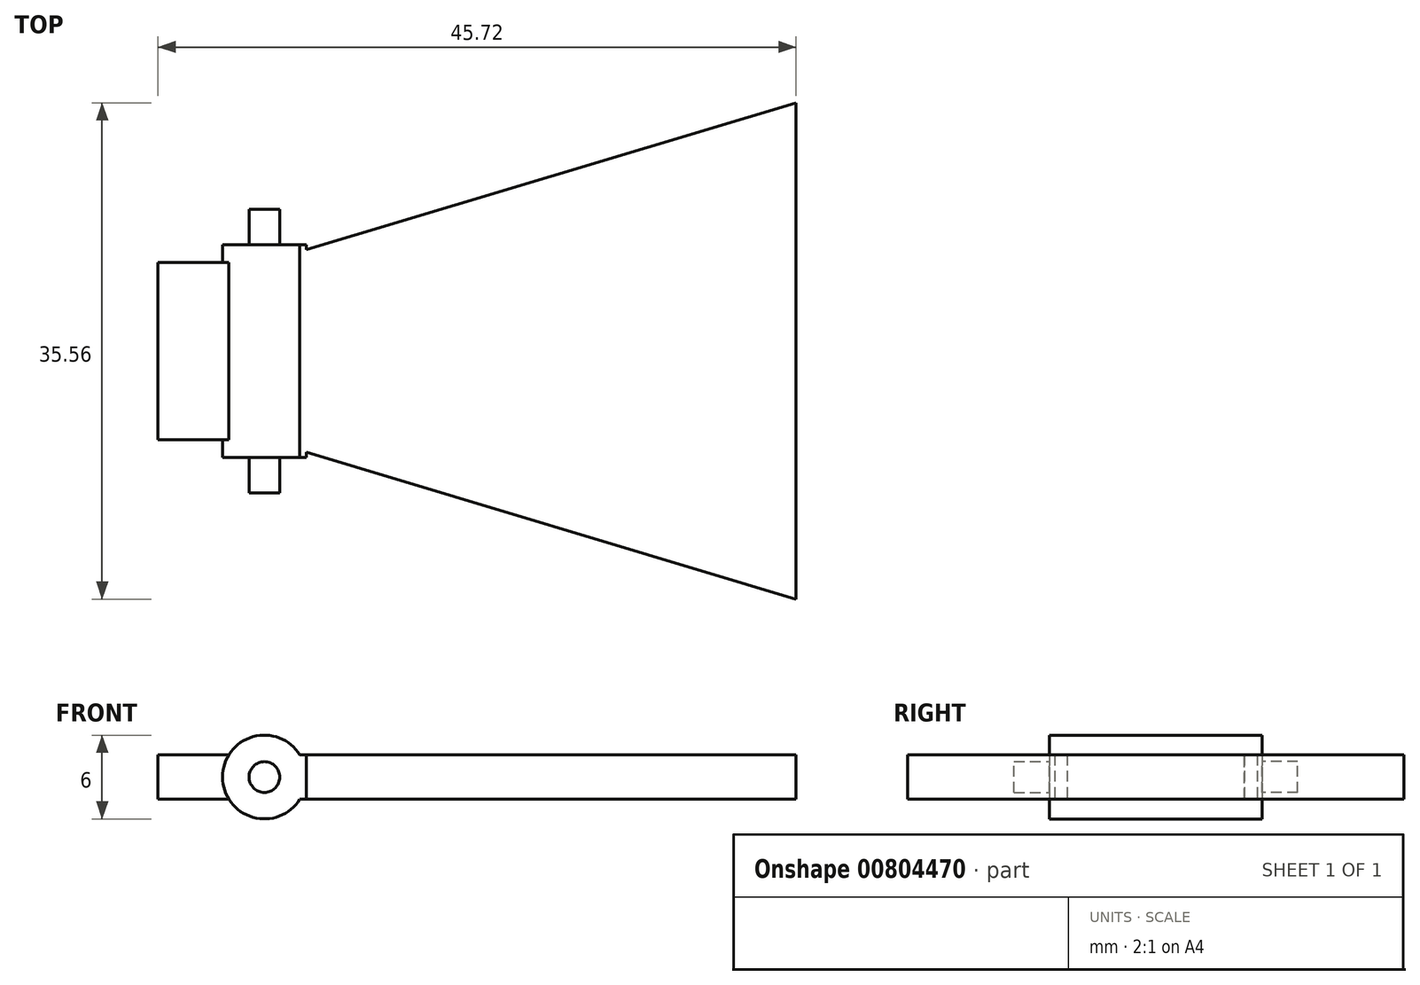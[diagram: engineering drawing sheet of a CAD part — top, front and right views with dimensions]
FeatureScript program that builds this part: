
annotation { "Feature Type Name" : "Feature", "Feature Type Description" : "" }
export const myFeature = defineFeature(function(context is Context, id is Id, definition is map)
    precondition{}
    {
        {
            var Q0;
            Q0=qCreatedBy(makeId("Top.planeOp"),FACE);
            var sketch = newSketch(context, id + "F0", { "sketchPlane" : qUnion([Q0])});
            skLineSegment(sketch, "E0", {"start": v(-25.02, 0) * mm, "end": v(-25.02, -6.35) * mm});
            skLineSegment(sketch, "E1", {"start": v(-25.02, -6.35) * mm, "end": v(13.08, -17.78) * mm});
            skLineSegment(sketch, "E2", {"start": v(13.08, -17.78) * mm, "end": v(13.08, 0) * mm});
            skLineSegment(sketch, "E3.MirrorCS", {"start": v(-25.02, 0) * mm, "end": v(-25.02, 6.35) * mm});
            skLineSegment(sketch, "E4.MirrorCS", {"start": v(-25.02, 6.35) * mm, "end": v(13.08, 17.78) * mm});
            skLineSegment(sketch, "E5.MirrorCS", {"start": v(13.08, 17.78) * mm, "end": v(13.08, 0) * mm});
            skLineSegment(sketch, "E6", {"start": v(-25.02, -6.35) * mm, "end": v(-32.64, -6.35) * mm});
            skLineSegment(sketch, "E7", {"start": v(-32.64, -6.35) * mm, "end": v(-32.64, 6.35) * mm});
            skLineSegment(sketch, "E8", {"start": v(-32.64, 6.35) * mm, "end": v(-25.02, 6.35) * mm});
            skLineSegment(sketch, "E9", {"start": v(-22.02, 6.35) * mm, "end": v(-22.02, -6.35) * mm});
            skLineSegment(sketch, "E10", {"start": v(-25.02, -6.35) * mm, "end": v(-25.02, -7.62) * mm});
            skLineSegment(sketch, "E11", {"start": v(-25.02, -7.62) * mm, "end": v(-22.02, -7.62) * mm});
            skLineSegment(sketch, "E12", {"start": v(-22.02, -7.62) * mm, "end": v(-22.02, -6.35) * mm});
            skLineSegment(sketch, "E13", {"start": v(-25.02, 6.35) * mm, "end": v(-22.02, 6.35) * mm});
            skLineSegment(sketch, "E14", {"start": v(-25.02, -6.35) * mm, "end": v(-22.02, -6.35) * mm});
            skLineSegment(sketch, "E15.MirrorCS", {"start": v(-25.02, 6.35) * mm, "end": v(-25.02, 7.62) * mm});
            skLineSegment(sketch, "E16.MirrorCS", {"start": v(-25.02, 7.62) * mm, "end": v(-22.02, 7.62) * mm});
            skLineSegment(sketch, "E17.MirrorCS", {"start": v(-22.02, 7.62) * mm, "end": v(-22.02, 6.35) * mm});
            skSolve(sketch);
        }
        {
            var Q0;
            Q0=makeQuery(id+"F0.imprint","IMPRINT",FACE,{"disambiguationData":[TD([[makeQuery(id+"F0.imprint","IMPRINT",EDGE,{"derivedFrom":sQuery(id+"F0.wireOp",EDGE,"E0")}),1.0]])]});
            var Q1;
            {var subQ0=sQuery(id+"F0.wireOp",EDGE,"E15.MirrorCS");Q1=makeQuery(id+"F0.imprint","IMPRINT",FACE,{"disambiguationData":[TD([[makeQuery(id+"F0.imprint","IMPRINT",EDGE,{"derivedFrom":subQ0}),-1.0]])]});}
            var Q2;
            {var subQ0=sQuery(id+"F0.wireOp",EDGE,"E10");Q2=makeQuery(id+"F0.imprint","IMPRINT",FACE,{"disambiguationData":[TD([[makeQuery(id+"F0.imprint","IMPRINT",EDGE,{"derivedFrom":subQ0}),1.0]])]});}
            var Q3;
            {var subQ0=sQuery(id+"F0.wireOp",EDGE,"E14");Q3=makeQuery(id+"F0.imprint","IMPRINT",FACE,{"disambiguationData":[TD([[makeQuery(id+"F0.imprint","IMPRINT",EDGE,{"derivedFrom":subQ0}),-1.0]])]});}
            var Q4;
            {var subQ0=sQuery(id+"F0.wireOp",EDGE,"E13");Q4=makeQuery(id+"F0.imprint","IMPRINT",FACE,{"disambiguationData":[TD([[makeQuery(id+"F0.imprint","IMPRINT",EDGE,{"derivedFrom":subQ0}),1.0]])]});}
            var Q5;
            Q5=sQuery(id+"F0.wireOp",EDGE,"E3.MirrorCS");
            revolve(context, id + "F1", {"surfaceOperationType" : NewSurfaceOperationType.NEW, "entities" : qUnion([Q0, Q1, Q2, Q3, Q4]), "axis" : qUnion([Q5]), "revolveType" : RevolveType.FULL});
        }
        {
            var Q0;
            Q0 = qSketchRegion(id + "F0", true);
            extrude(context, id + "F2", {"entities" : qUnion([Q0]), "operationType" : NewBodyOperationType.ADD, "endBound" : BoundingType.SYMMETRIC, "depth" : 3.17 * mm, "offsetDistance" : 25.4 * mm});
        }
        {
            var Q0;
            {var subQ0=sQuery(id+"F0.wireOp",EDGE,"E11");Q0=makeQuery(id+"F2.boolean.opBoolean","MERGE",FACE,{"derivedFrom":[makeQuery(id+"F1.opRevolve","SWEPT_FACE",FACE,{"disambiguationData":[OSD([subQ0])]}),makeQuery(id+"F2.opExtrude","SWEPT_FACE",FACE,{"disambiguationData":[OSD([subQ0])]})]});}
            var sketch = newSketch(context, id + "F3", { "sketchPlane" : qUnion([Q0])});
            skCircle(sketch, "E18", {"center": v(-25.02, 0) * mm, "radius": 1.1 * mm});
            skSolve(sketch);
        }
        {
            var Q0;
            {var subQ0=sQuery(id+"F0.wireOp",EDGE,"E16.MirrorCS");Q0=makeQuery(id+"F2.boolean.opBoolean","MERGE",FACE,{"derivedFrom":[makeQuery(id+"F1.opRevolve","SWEPT_FACE",FACE,{"disambiguationData":[OSD([subQ0])]}),makeQuery(id+"F2.opExtrude","SWEPT_FACE",FACE,{"disambiguationData":[OSD([subQ0])]})]});}
            var sketch = newSketch(context, id + "F4", { "sketchPlane" : qUnion([Q0])});
            skCircle(sketch, "E19", {"center": v(25.02, 0) * mm, "radius": 1.1 * mm});
            skSolve(sketch);
        }
        {
            var Q0;
            Q0=makeQuery(id+"F4.imprint","IMPRINT",FACE,{"disambiguationData":[TD([[makeQuery(id+"F4.imprint","IMPRINT",EDGE,{"derivedFrom":sQuery(id+"F4.wireOp",EDGE,"E19")}),1.0]])]});
            extrude(context, id + "F5", {"entities" : qUnion([Q0]), "operationType" : NewBodyOperationType.ADD, "depth" : 2.54 * mm, "offsetDistance" : 25.4 * mm});
        }
        {
            var Q0;
            Q0=makeQuery(id+"F3.imprint","IMPRINT",FACE,{"disambiguationData":[TD([[makeQuery(id+"F3.imprint","IMPRINT",EDGE,{"derivedFrom":sQuery(id+"F3.wireOp",EDGE,"E18")}),1.0]])]});
            extrude(context, id + "F6", {"entities" : qUnion([Q0]), "operationType" : NewBodyOperationType.ADD, "depth" : 2.54 * mm, "offsetDistance" : 25.4 * mm});
        }
    });
